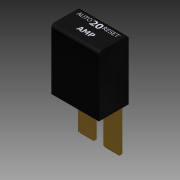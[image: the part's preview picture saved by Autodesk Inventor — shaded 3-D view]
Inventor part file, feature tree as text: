
AUTODESK INVENTOR PART (.ipt)
format: ipt  version: 2014 (Build 180170000, 170)  size: 450,048 bytes
history: native  units: in
note: dims shown in document units (in); Inventor stores cm internally (conversion verified against a paired STEP export)
features: sketch x6, extrude x4, plane x3, emboss x2, fillet x1, mirror x1
ambient origin geometry x8: Origin, YZ Plane, XZ Plane, XY Plane, X Axis, Y Axis, Z Axis, Center Point
bodies: Solid1 (feature_tree)
feature tree (17):
  extrude  "Extrusion1"  Depth=0.39in
  fillet  "Fillet1"  Radius=0.78in
  extrude  "Extrusion3"  Depth=0.212in
  extrude  "Extrusion4"  Depth=0.0585in
  extrude  "Extrusion5"  Depth=0.57in TaperAngle=0.0deg
  plane  "Work Plane1"
  mirror  "Mirror1"
  plane  "Work Plane2"
  emboss  "Emboss1"
  plane  "Work Plane4"
  emboss  "Emboss3"
  sketch  "Sketch1"  dims[d0=0.62in d1=0.39in d2=0.78in d3=0.0in]
  sketch  "Sketch2"  dims[d4=0.01in d5=0.05in d6=0.212in]
  sketch  "Sketch3"  dims[d8=0.031in d13=0.0585in]
  sketch  "Sketch4"  dims[d14=0.57in d15=0.0in d16=0.57in d17=0.0in]
  sketch  "Sketch6"  dims[d18=0.023in]
  sketch  "Sketch8"  dims[d19=0.023in d20=0.023in d21=0.57in d22=0.0in d26=0.1875in d27=0.0001in d28=0.0in d32=0.1875in d33=0.0001in d34=0.0in]
